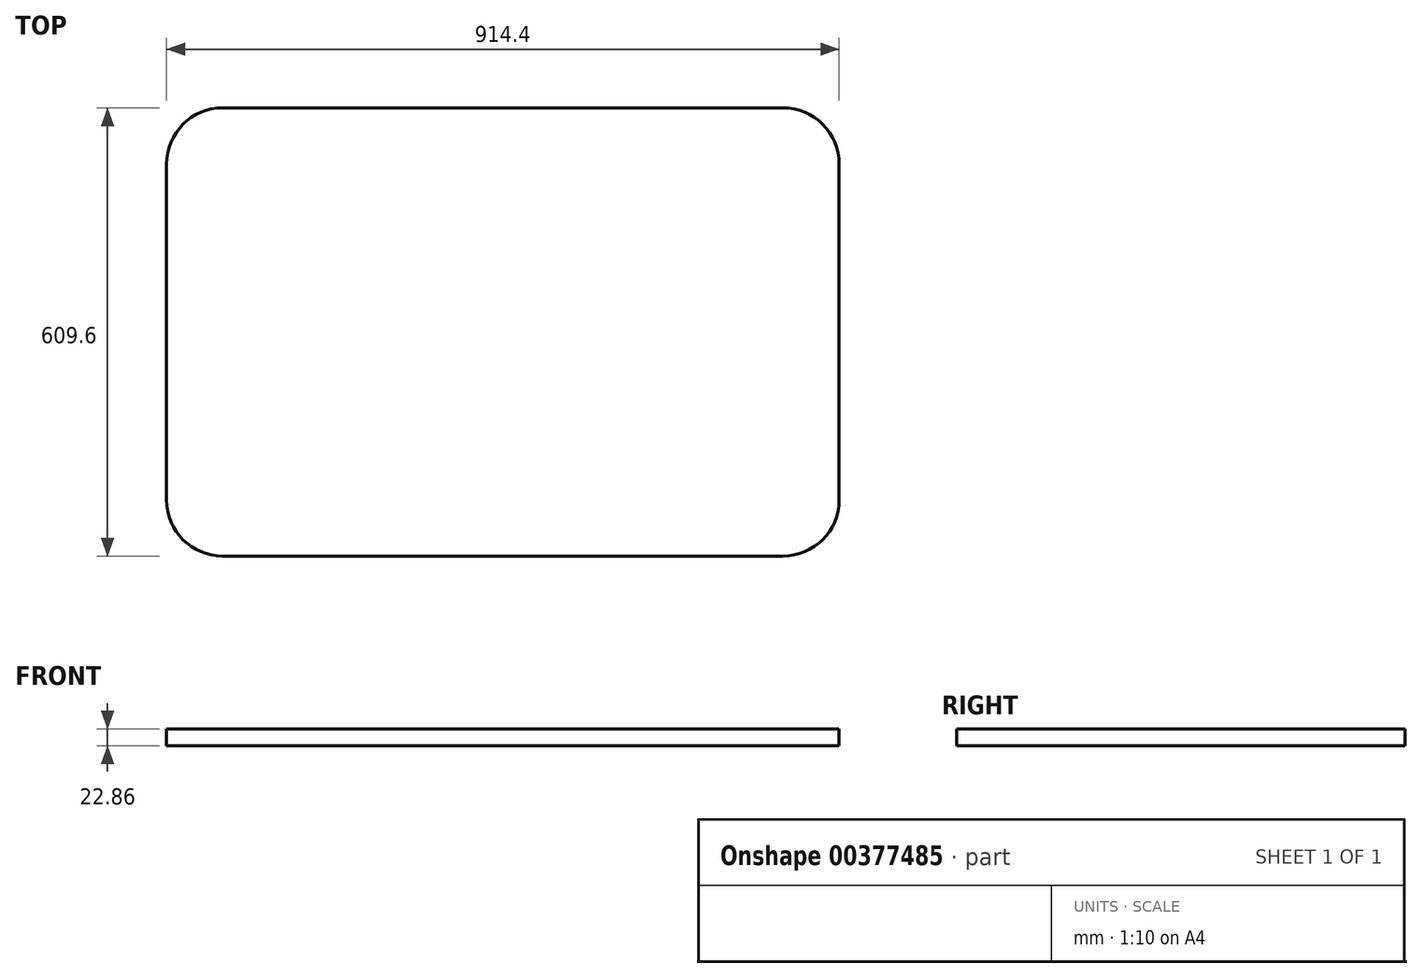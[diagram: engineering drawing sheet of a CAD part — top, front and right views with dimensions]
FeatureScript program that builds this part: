
annotation { "Feature Type Name" : "Feature", "Feature Type Description" : "" }
export const myFeature = defineFeature(function(context is Context, id is Id, definition is map)
    precondition{}
    {
        {
            var Q0;
            Q0=qCreatedBy(makeId("Top.planeOp"),FACE);
            var sketch = newSketch(context, id + "F0", { "sketchPlane" : qUnion([Q0])});
            skLineSegment(sketch, "E0.bottom", {"start": v(76.2, 0) * mm, "end": v(838.2, 0) * mm});
            skLineSegment(sketch, "E0.top", {"start": v(76.2, 609.6) * mm, "end": v(838.2, 609.6) * mm});
            skLineSegment(sketch, "E0.left", {"start": v(0, 76.2) * mm, "end": v(0, 533.4) * mm});
            skLineSegment(sketch, "E0.right", {"start": v(914.4, 76.2) * mm, "end": v(914.4, 533.4) * mm});
            skPoint(sketch, "E1.visualSharp", {"position": v(0, 609.6) * mm});
            skArc(sketch, "E1.filletArc", {"start": v(76.2, 609.6) * mm, "mid": v(22.32, 587.28) * mm, "end": v(0, 533.4) * mm});
            skPoint(sketch, "E2.visualSharp", {"position": v(914.4, 609.6) * mm});
            skArc(sketch, "E2.filletArc", {"start": v(914.4, 533.4) * mm, "mid": v(892.08, 587.28) * mm, "end": v(838.2, 609.6) * mm});
            skPoint(sketch, "E3.visualSharp", {"position": v(914.4, 0) * mm});
            skArc(sketch, "E3.filletArc", {"start": v(838.2, 0) * mm, "mid": v(892.08, 22.32) * mm, "end": v(914.4, 76.2) * mm});
            skPoint(sketch, "E4.visualSharp", {"position": v(0, 0) * mm});
            skArc(sketch, "E4.filletArc", {"start": v(0, 76.2) * mm, "mid": v(22.32, 22.32) * mm, "end": v(76.2, 0) * mm});
            skSolve(sketch);
        }
        {
            var Q0;
            Q0 = qSketchRegion(id + "F0", true);
            extrude(context, id + "F1", {"entities" : qUnion([Q0]), "depth" : 22.86 * mm, "offsetDistance" : 25.4 * mm});
        }
    });
